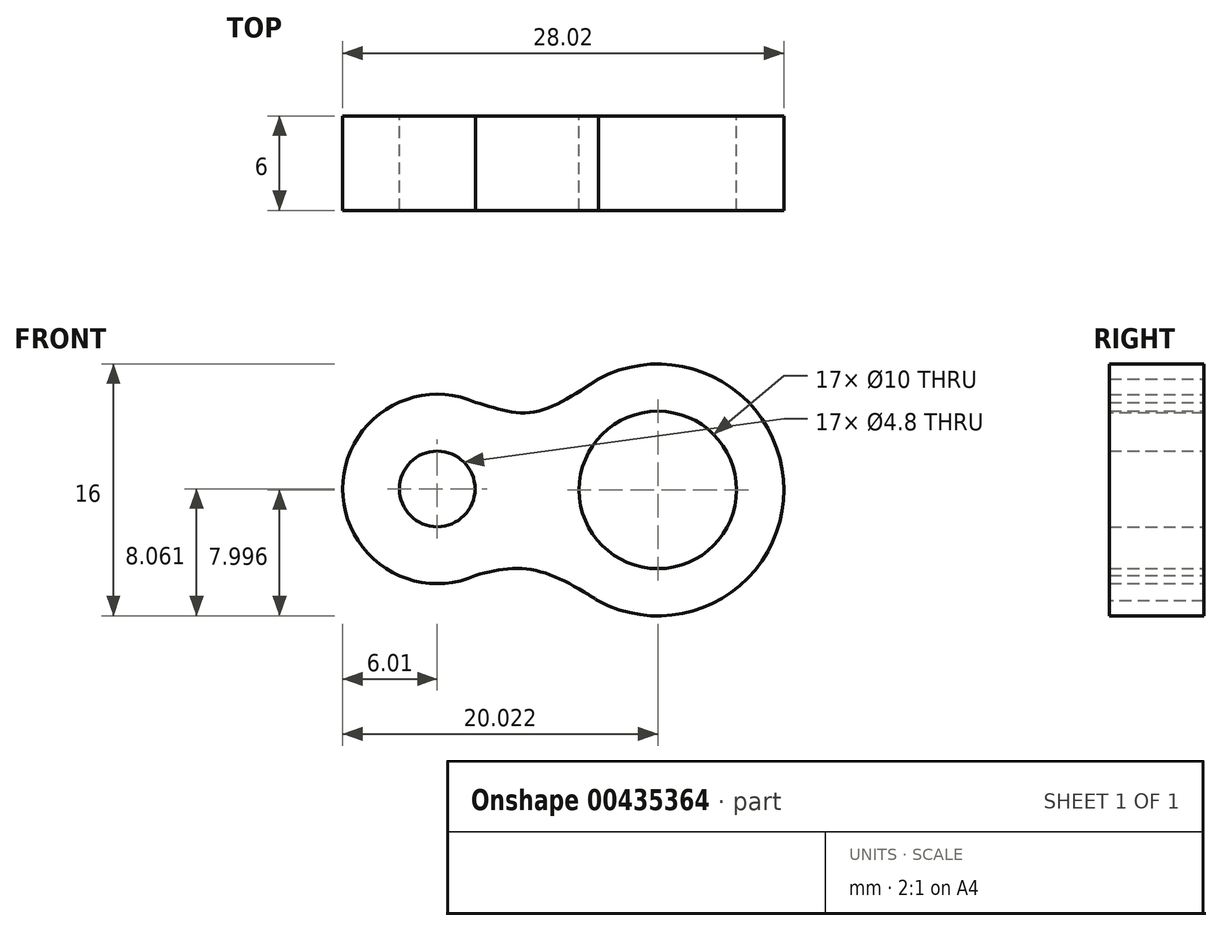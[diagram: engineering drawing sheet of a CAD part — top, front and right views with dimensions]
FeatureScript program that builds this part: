
annotation { "Feature Type Name" : "Feature", "Feature Type Description" : "" }
export const myFeature = defineFeature(function(context is Context, id is Id, definition is map)
    precondition{}
    {
        {
            var Q0;
            Q0=qCreatedBy(makeId("Front.planeOp"),FACE);
            var sketch = newSketch(context, id + "F0", { "sketchPlane" : qUnion([Q0])});
            skCircle(sketch, "E0", {"center": v(7, 0.07) * mm, "radius": 5 * mm});
            skCircle(sketch, "E1", {"center": v(-7.01, 0.13) * mm, "radius": 2.4 * mm});
            skLineSegment(sketch, "E2", {"start": v(-1, 0) * mm, "end": v(-1.3, 0) * mm});
            skPoint(sketch, "E3.end.orphan", {"position": v(7, -7.93) * mm});
            skPoint(sketch, "E4.end.orphan", {"position": v(-7.01, -5.88) * mm});
            skArc(sketch, "E5", {"start": v(2.3, -6.4) * mm, "mid": v(15, 0.19) * mm, "end": v(2.1, 6.4) * mm});
            skLineSegment(sketch, "E6", {"start": v(-1, 0.13) * mm, "end": v(-1, 0.13) * mm});
            skLineSegment(sketch, "E7", {"start": v(-1, 0) * mm, "end": v(-1, 0.13) * mm});
            skFitSpline(sketch, "E8", {"points": [v(-4.58, 5.63) * mm, v(-1, 5) * mm, v(3.23, 7.12) * mm], "startDerivative": vector(7.58, -2.19) * mm, "endDerivative": vector(8, 5.16) * mm});
            skFitSpline(sketch, "E9", {"points": [v(-4.58, -5.37) * mm, v(-1, -5) * mm, v(3.23, -6.99) * mm], "startDerivative": vector(7.58, 2.18) * mm, "endDerivative": vector(8, -5.16) * mm});
            skArc(sketch, "E10.trimOffspring", {"start": v(-4.58, 5.63) * mm, "mid": v(-13.02, 0.13) * mm, "end": v(-4.58, -5.37) * mm});
            skPoint(sketch, "E11.end.orphan", {"position": v(-1.3, 0) * mm});
            skPoint(sketch, "E12.orphan", {"position": v(-4.61, 0) * mm});
            skPoint(sketch, "E13.orphan", {"position": v(2, 0) * mm});
            skSolve(sketch);
        }
        {
            var Q0;
            Q0=makeQuery(id+"F0.imprint","IMPRINT",FACE,{"disambiguationData":[TD([[makeQuery(id+"F0.imprint","IMPRINT",EDGE,{"derivedFrom":sQuery(id+"F0.wireOp",EDGE,"E0")}),-1.0]])]});
            extrude(context, id + "F1", {"entities" : qUnion([Q0]), "depth" : 6 * mm, "offsetDistance" : 25 * mm});
        }
    });
